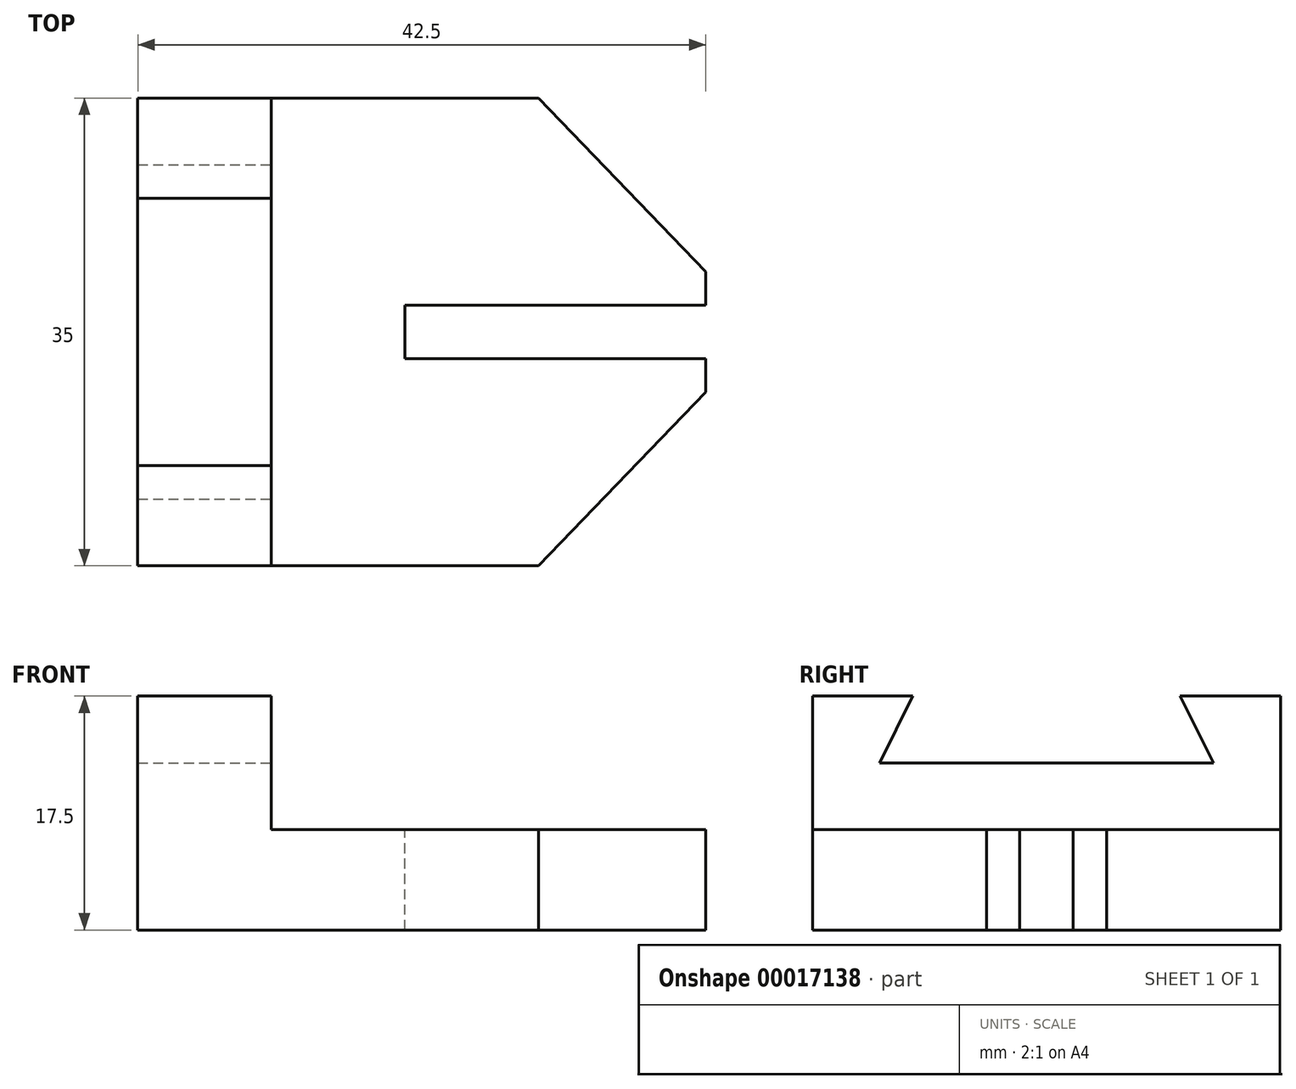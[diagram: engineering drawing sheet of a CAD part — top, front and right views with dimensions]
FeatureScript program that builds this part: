
annotation { "Feature Type Name" : "Feature", "Feature Type Description" : "" }
export const myFeature = defineFeature(function(context is Context, id is Id, definition is map)
    precondition{}
    {
        {
            var Q0;
            Q0=qCreatedBy(makeId("Top.planeOp"),FACE);
            var sketch = newSketch(context, id + "F0", { "sketchPlane" : qUnion([Q0])});
            skLineSegment(sketch, "E0.bottom", {"start": v(-37.67, 31.8) * mm, "end": v(4.83, 31.8) * mm});
            skLineSegment(sketch, "E0.top", {"start": v(-37.67, -3.2) * mm, "end": v(4.83, -3.2) * mm});
            skLineSegment(sketch, "E0.left", {"start": v(-37.67, 31.8) * mm, "end": v(-37.67, -3.2) * mm});
            skLineSegment(sketch, "E0.right", {"start": v(4.83, 31.8) * mm, "end": v(4.83, -3.2) * mm});
            skSolve(sketch);
        }
        {
            var Q0;
            Q0=makeQuery(id+"F0.imprint","IMPRINT",FACE,{"disambiguationData":[TD([[makeQuery(id+"F0.imprint","IMPRINT",EDGE,{"derivedFrom":sQuery(id+"F0.wireOp",EDGE,"E0.bottom")}),-1.0]])]});
            extrude(context, id + "F1", {"entities" : qUnion([Q0]), "depth" : 7.5 * mm});
        }
        {
            var Q0;
            Q0=makeQuery(id+"F1.opExtrude","CAP_FACE",FACE,{"disambiguationData":[OSD([sQuery(id+"F0.wireOp",EDGE,"E0.bottom"),sQuery(id+"F0.wireOp",EDGE,"E0.top"),sQuery(id+"F0.wireOp",EDGE,"E0.left"),sQuery(id+"F0.wireOp",EDGE,"E0.right")])],"isStart":false});
            var sketch = newSketch(context, id + "F2", { "sketchPlane" : qUnion([Q0])});
            skLineSegment(sketch, "E1", {"start": v(4.83, 9.8) * mm, "end": v(4.83, -3.2) * mm});
            skLineSegment(sketch, "E2", {"start": v(4.83, -3.2) * mm, "end": v(-7.67, -3.2) * mm});
            skLineSegment(sketch, "E3", {"start": v(-7.67, -3.2) * mm, "end": v(4.83, 9.8) * mm});
            skLineSegment(sketch, "E4", {"start": v(4.83, 31.8) * mm, "end": v(-7.67, 31.8) * mm});
            skLineSegment(sketch, "E5", {"start": v(-7.67, 31.8) * mm, "end": v(4.83, 18.8) * mm});
            skLineSegment(sketch, "E6", {"start": v(4.83, 18.8) * mm, "end": v(4.83, 31.8) * mm});
            skSolve(sketch);
        }
        {
            var Q0;
            Q0=makeQuery(id+"F2.imprint","IMPRINT",FACE,{"disambiguationData":[TD([[makeQuery(id+"F2.imprint","IMPRINT",EDGE,{"derivedFrom":sQuery(id+"F2.wireOp",EDGE,"E4")}),-1.0]])]});
            extrude(context, id + "F3", {"entities" : qUnion([Q0]), "operationType" : NewBodyOperationType.REMOVE, "endBound" : BoundingType.THROUGH_ALL, "oppositeDirection" : true, "depth" : 25 * mm});
        }
        {
            var Q0;
            Q0 = qSketchRegion(id + "F2", true);
            extrude(context, id + "F4", {"entities" : qUnion([Q0]), "operationType" : NewBodyOperationType.REMOVE, "endBound" : BoundingType.THROUGH_ALL, "oppositeDirection" : true, "depth" : 25 * mm});
        }
        {
            var Q0;
            Q0=makeQuery(id+"F1.opExtrude","CAP_FACE",FACE,{"disambiguationData":[OSD([sQuery(id+"F0.wireOp",EDGE,"E0.bottom"),sQuery(id+"F0.wireOp",EDGE,"E0.top"),sQuery(id+"F0.wireOp",EDGE,"E0.left"),sQuery(id+"F0.wireOp",EDGE,"E0.right")])],"isStart":false});
            var sketch = newSketch(context, id + "F5", { "sketchPlane" : qUnion([Q0])});
            skLineSegment(sketch, "E7", {"start": v(4.83, 16.3) * mm, "end": v(-17.67, 16.3) * mm});
            skLineSegment(sketch, "E8", {"start": v(-17.67, 16.3) * mm, "end": v(-17.67, 12.3) * mm});
            skLineSegment(sketch, "E9", {"start": v(-17.67, 12.3) * mm, "end": v(4.83, 12.3) * mm});
            skLineSegment(sketch, "E10", {"start": v(4.83, 12.3) * mm, "end": v(4.83, 16.3) * mm});
            skSolve(sketch);
        }
        {
            var Q0;
            Q0=makeQuery(id+"F5.imprint","IMPRINT",FACE,{"disambiguationData":[TD([[makeQuery(id+"F5.imprint","IMPRINT",EDGE,{"derivedFrom":sQuery(id+"F5.wireOp",EDGE,"E7")}),1.0]])]});
            extrude(context, id + "F6", {"entities" : qUnion([Q0]), "operationType" : NewBodyOperationType.REMOVE, "endBound" : BoundingType.THROUGH_ALL, "oppositeDirection" : true, "depth" : 25 * mm});
        }
        {
            var Q0;
            Q0=makeQuery(id+"F1.opExtrude","CAP_FACE",FACE,{"disambiguationData":[OSD([sQuery(id+"F0.wireOp",EDGE,"E0.bottom"),sQuery(id+"F0.wireOp",EDGE,"E0.top"),sQuery(id+"F0.wireOp",EDGE,"E0.left"),sQuery(id+"F0.wireOp",EDGE,"E0.right")])],"isStart":false});
            var sketch = newSketch(context, id + "F7", { "sketchPlane" : qUnion([Q0])});
            skLineSegment(sketch, "E11.bottom", {"start": v(-37.67, 31.8) * mm, "end": v(-27.67, 31.8) * mm});
            skLineSegment(sketch, "E11.top", {"start": v(-37.67, -3.2) * mm, "end": v(-27.67, -3.2) * mm});
            skLineSegment(sketch, "E11.left", {"start": v(-37.67, 31.8) * mm, "end": v(-37.67, -3.2) * mm});
            skLineSegment(sketch, "E11.right", {"start": v(-27.67, 31.8) * mm, "end": v(-27.67, -3.2) * mm});
            skSolve(sketch);
        }
        {
            var Q0;
            Q0=makeQuery(id+"F7.imprint","IMPRINT",FACE,{"disambiguationData":[TD([[makeQuery(id+"F7.imprint","IMPRINT",EDGE,{"derivedFrom":sQuery(id+"F7.wireOp",EDGE,"E11.bottom")}),-1.0]])]});
            extrude(context, id + "F8", {"entities" : qUnion([Q0]), "operationType" : NewBodyOperationType.ADD, "depth" : 10 * mm});
        }
        {
            var Q0;
            Q0=makeQuery(id+"F8.opExtrude","SWEPT_FACE",FACE,{"disambiguationData":[OSD([sQuery(id+"F7.wireOp",EDGE,"E11.right")])]});
            var sketch = newSketch(context, id + "F9", { "sketchPlane" : qUnion([Q0])});
            skLineSegment(sketch, "E12", {"start": v(4.3, 17.5) * mm, "end": v(1.8, 12.5) * mm});
            skLineSegment(sketch, "E13", {"start": v(1.8, 12.5) * mm, "end": v(26.8, 12.5) * mm});
            skLineSegment(sketch, "E14", {"start": v(26.8, 12.5) * mm, "end": v(24.3, 17.5) * mm});
            skLineSegment(sketch, "E15", {"start": v(24.3, 17.5) * mm, "end": v(4.3, 17.5) * mm});
            skSolve(sketch);
        }
        {
            var Q0;
            Q0=makeQuery(id+"F9.imprint","IMPRINT",FACE,{"disambiguationData":[TD([[makeQuery(id+"F9.imprint","IMPRINT",EDGE,{"derivedFrom":sQuery(id+"F9.wireOp",EDGE,"E12")}),1.0]])]});
            extrude(context, id + "F10", {"entities" : qUnion([Q0]), "operationType" : NewBodyOperationType.REMOVE, "endBound" : BoundingType.THROUGH_ALL, "oppositeDirection" : true, "depth" : 25 * mm});
        }
    });
